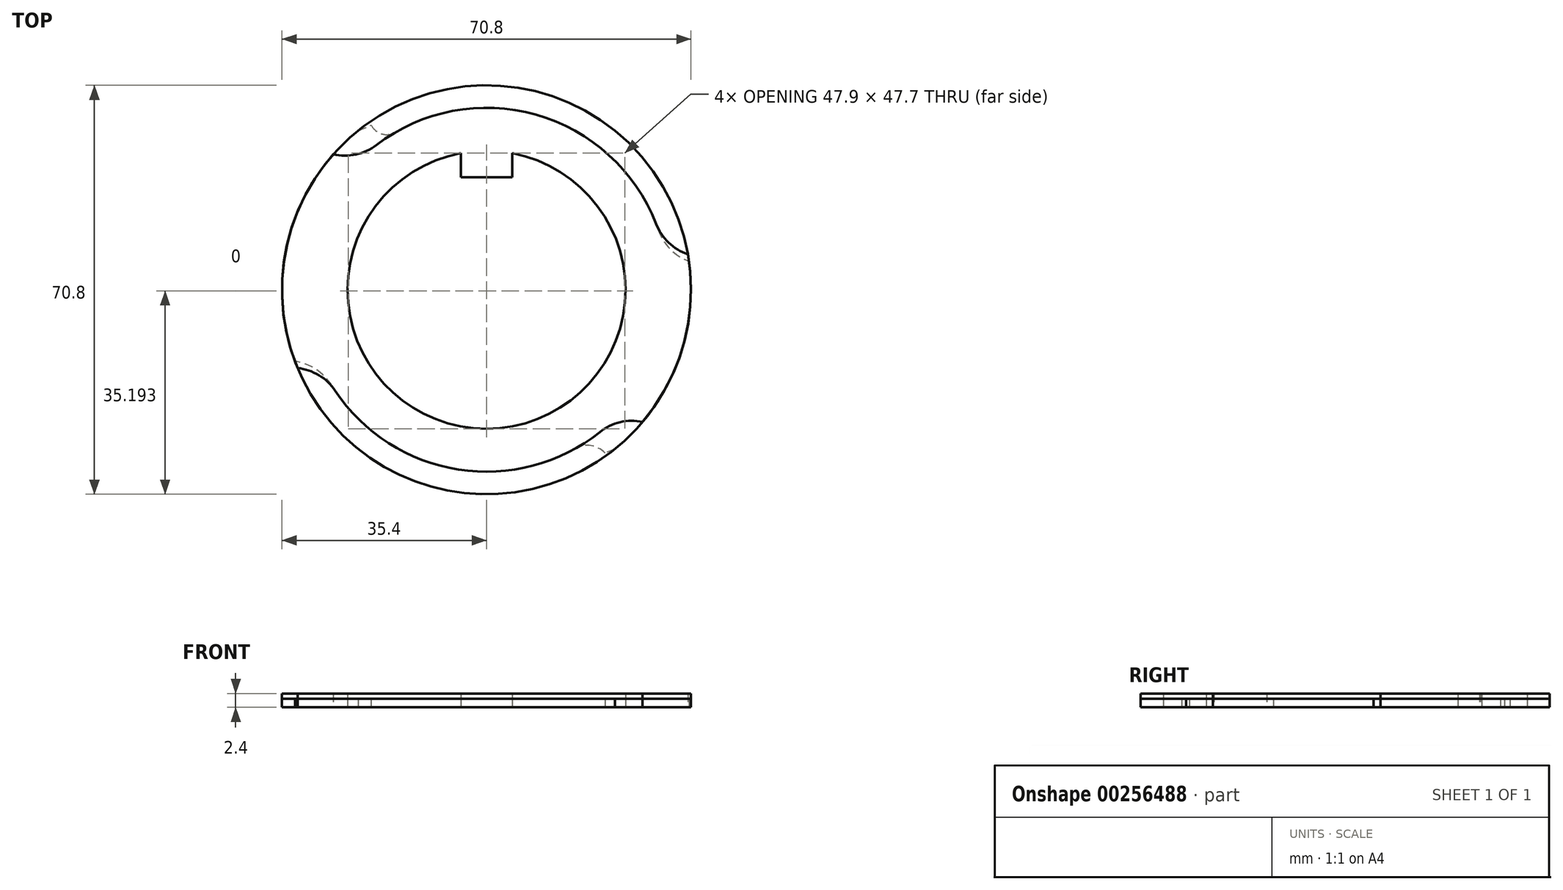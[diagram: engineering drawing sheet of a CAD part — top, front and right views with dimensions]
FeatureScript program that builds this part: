
annotation { "Feature Type Name" : "Feature", "Feature Type Description" : "" }
export const myFeature = defineFeature(function(context is Context, id is Id, definition is map)
    precondition{}
    {
        {
            var Q0;
            Q0=qCreatedBy(makeId("Top.planeOp"),FACE);
            var sketch = newSketch(context, id + "F0", { "sketchPlane" : qUnion([Q0])});
            skArc(sketch, "E0", {"start": v(7.4, -9.19) * mm, "mid": v(3.12, 11.38) * mm, "end": v(-11.05, -4.13) * mm});
            skArc(sketch, "E1", {"start": v(-1.48, 7.88) * mm, "mid": v(0, -8.02) * mm, "end": v(1.48, 7.88) * mm});
            skLineSegment(sketch, "E2", {"start": v(-1.48, 6.5) * mm, "end": v(1.48, 6.5) * mm});
            skPoint(sketch, "E3", {"position": v(0, 6.5) * mm});
            skLineSegment(sketch, "E4", {"start": v(1.48, 6.5) * mm, "end": v(1.48, 7.88) * mm});
            skLineSegment(sketch, "E5", {"start": v(-1.48, 6.5) * mm, "end": v(-1.48, 7.88) * mm});
            skLineSegment(sketch, "E6", {"start": v(0, 0) * mm, "end": v(6.94, -9.55) * mm, "construction": true});
            skLineSegment(sketch, "E7", {"start": v(0, 0) * mm, "end": v(-11.05, -4.13) * mm, "construction": true});
            skArc(sketch, "E8", {"start": v(-8.93, -5.52) * mm, "mid": v(-2.62, -10.17) * mm, "end": v(5.14, -9.15) * mm});
            skArc(sketch, "E9", {"start": v(-8.93, -5.52) * mm, "mid": v(-9.84, -4.6) * mm, "end": v(-11.05, -4.13) * mm});
            skArc(sketch, "E10", {"start": v(6.84, -9.43) * mm, "mid": v(6.04, -9) * mm, "end": v(5.14, -9.15) * mm});
            skLineSegment(sketch, "E11", {"start": v(7.4, -9.19) * mm, "end": v(6.84, -9.43) * mm});
            skSolve(sketch);
        }
        {
            var Q0;
            Q0=makeQuery(id+"F0.imprint","IMPRINT",FACE,{"disambiguationData":[TD([[makeQuery(id+"F0.imprint","IMPRINT",EDGE,{"derivedFrom":sQuery(id+"F0.wireOp",EDGE,"E0")}),1.0]])]});
            extrude(context, id + "F1", {"entities" : qUnion([Q0]), "depth" : 0.5 * mm});
        }
        {
            var Q0;
            Q0=qCreatedBy(makeId("Top.planeOp"),FACE);
            var sketch = newSketch(context, id + "F2", { "sketchPlane" : qUnion([Q0])});
            skArc(sketch, "E12", {"start": v(9, -7.62) * mm, "mid": v(1.82, 11.66) * mm, "end": v(-10.9, -4.52) * mm});
            skArc(sketch, "E13", {"start": v(-1.48, 7.88) * mm, "mid": v(0, -8.02) * mm, "end": v(1.48, 7.88) * mm});
            skLineSegment(sketch, "E14", {"start": v(-1.48, 6.5) * mm, "end": v(1.48, 6.5) * mm});
            skPoint(sketch, "E15", {"position": v(0, 6.5) * mm});
            skLineSegment(sketch, "E16", {"start": v(-1.48, 6.5) * mm, "end": v(-1.48, 7.88) * mm});
            skLineSegment(sketch, "E17", {"start": v(1.48, 6.5) * mm, "end": v(1.48, 7.88) * mm});
            skLineSegment(sketch, "E18", {"start": v(0, 0) * mm, "end": v(9, -7.62) * mm, "construction": true});
            skLineSegment(sketch, "E19", {"start": v(0, 0) * mm, "end": v(-10.9, -4.52) * mm, "construction": true});
            skArc(sketch, "E20", {"start": v(-8.73, -5.83) * mm, "mid": v(-1.62, -10.37) * mm, "end": v(6.54, -8.22) * mm});
            skArc(sketch, "E21", {"start": v(-8.73, -5.83) * mm, "mid": v(-9.67, -4.93) * mm, "end": v(-10.9, -4.52) * mm});
            skArc(sketch, "E22", {"start": v(9, -7.62) * mm, "mid": v(7.7, -7.65) * mm, "end": v(6.54, -8.22) * mm});
            skPoint(sketch, "E23.orphan", {"position": v(-9.7, -4.02) * mm});
            skPoint(sketch, "E24.orphan", {"position": v(8.01, -6.78) * mm});
            skSolve(sketch);
        }
        {
            var Q0;
            Q0=makeQuery(id+"F2.imprint","IMPRINT",FACE,{"disambiguationData":[TD([[makeQuery(id+"F2.imprint","IMPRINT",EDGE,{"derivedFrom":sQuery(id+"F2.wireOp",EDGE,"E12")}),1.0]])]});
            extrude(context, id + "F3", {"entities" : qUnion([Q0]), "depth" : 0.8 * mm});
        }
        {
            var Q0;
            Q0=qCreatedBy(makeId("Top.planeOp"),FACE);
            var sketch = newSketch(context, id + "F4", { "sketchPlane" : qUnion([Q0])});
            skArc(sketch, "E25", {"start": v(-1.48, 7.88) * mm, "mid": v(0, -8.02) * mm, "end": v(1.48, 7.88) * mm});
            skArc(sketch, "E26", {"start": v(-7.4, 9.19) * mm, "mid": v(-4.34, -10.97) * mm, "end": v(11.69, 1.64) * mm});
            skLineSegment(sketch, "E27", {"start": v(-1.48, 6.5) * mm, "end": v(1.48, 6.5) * mm});
            skPoint(sketch, "E28", {"position": v(0, 6.5) * mm});
            skLineSegment(sketch, "E29", {"start": v(-1.48, 6.5) * mm, "end": v(-1.48, 7.88) * mm});
            skLineSegment(sketch, "E30", {"start": v(1.48, 6.5) * mm, "end": v(1.48, 7.88) * mm});
            skLineSegment(sketch, "E31", {"start": v(0, 0) * mm, "end": v(-6.73, 9.7) * mm, "construction": true});
            skLineSegment(sketch, "E32", {"start": v(0, 0) * mm, "end": v(11.69, 1.64) * mm, "construction": true});
            skArc(sketch, "E33", {"start": v(9.91, 3.46) * mm, "mid": v(3.65, 9.84) * mm, "end": v(-5.26, 9.09) * mm});
            skArc(sketch, "E34", {"start": v(-6.65, 9.5) * mm, "mid": v(-6.05, 9) * mm, "end": v(-5.26, 9.09) * mm});
            skArc(sketch, "E35", {"start": v(9.91, 3.46) * mm, "mid": v(10.6, 2.35) * mm, "end": v(11.69, 1.64) * mm});
            skLineSegment(sketch, "E36", {"start": v(-7.4, 9.19) * mm, "end": v(-6.65, 9.5) * mm});
            skSolve(sketch);
        }
        {
            var Q0;
            Q0=makeQuery(id+"F4.imprint","IMPRINT",FACE,{"disambiguationData":[TD([[makeQuery(id+"F4.imprint","IMPRINT",EDGE,{"derivedFrom":sQuery(id+"F4.wireOp",EDGE,"E25")}),-1.0]])]});
            extrude(context, id + "F5", {"entities" : qUnion([Q0]), "depth" : 0.5 * mm});
        }
        {
            var Q0;
            Q0=qCreatedBy(makeId("Top.planeOp"),FACE);
            var sketch = newSketch(context, id + "F6", { "sketchPlane" : qUnion([Q0])});
            skArc(sketch, "E37", {"start": v(-1.48, 7.88) * mm, "mid": v(0, -8.02) * mm, "end": v(1.48, 7.88) * mm});
            skArc(sketch, "E38", {"start": v(-8.84, 7.82) * mm, "mid": v(-3.2, -11.36) * mm, "end": v(11.62, 2.05) * mm});
            skLineSegment(sketch, "E39", {"start": v(-1.48, 6.5) * mm, "end": v(1.48, 6.5) * mm});
            skPoint(sketch, "E40", {"position": v(0, 6.5) * mm});
            skLineSegment(sketch, "E41", {"start": v(-1.48, 6.5) * mm, "end": v(-1.48, 7.88) * mm});
            skLineSegment(sketch, "E42", {"start": v(1.48, 6.5) * mm, "end": v(1.48, 7.88) * mm});
            skLineSegment(sketch, "E43", {"start": v(0, 0) * mm, "end": v(-8.84, 7.82) * mm, "construction": true});
            skLineSegment(sketch, "E44", {"start": v(0, 0) * mm, "end": v(11.62, 2.05) * mm, "construction": true});
            skArc(sketch, "E45", {"start": v(9.79, 3.8) * mm, "mid": v(2.85, 10.1) * mm, "end": v(-6.36, 8.36) * mm});
            skArc(sketch, "E46", {"start": v(-8.84, 7.82) * mm, "mid": v(-7.54, 7.81) * mm, "end": v(-6.36, 8.36) * mm});
            skArc(sketch, "E47", {"start": v(9.79, 3.8) * mm, "mid": v(10.5, 2.72) * mm, "end": v(11.62, 2.05) * mm});
            skSolve(sketch);
        }
        {
            var Q0;
            Q0=makeQuery(id+"F6.imprint","IMPRINT",FACE,{"disambiguationData":[TD([[makeQuery(id+"F6.imprint","IMPRINT",EDGE,{"derivedFrom":sQuery(id+"F6.wireOp",EDGE,"E37")}),-1.0]])]});
            extrude(context, id + "F7", {"entities" : qUnion([Q0]), "depth" : 0.8 * mm});
        }
        {
            var Q0;
            Q0=makeQuery(id+"F1.opExtrude","SWEPT_BODY",BODY,{"disambiguationData":[OSD([sQuery(id+"F0.wireOp",EDGE,"E0"),sQuery(id+"F0.wireOp",EDGE,"E1"),sQuery(id+"F0.wireOp",EDGE,"E2"),sQuery(id+"F0.wireOp",EDGE,"E4"),sQuery(id+"F0.wireOp",EDGE,"E5"),sQuery(id+"F0.wireOp",EDGE,"E8"),sQuery(id+"F0.wireOp",EDGE,"E9"),sQuery(id+"F0.wireOp",EDGE,"E10"),sQuery(id+"F0.wireOp",EDGE,"E11")])]});
            var Q1;
            Q1=makeQuery(id+"F3.opExtrude","SWEPT_BODY",BODY,{"disambiguationData":[OSD([sQuery(id+"F2.wireOp",EDGE,"E12"),sQuery(id+"F2.wireOp",EDGE,"E13"),sQuery(id+"F2.wireOp",EDGE,"E14"),sQuery(id+"F2.wireOp",EDGE,"E16"),sQuery(id+"F2.wireOp",EDGE,"E17"),sQuery(id+"F2.wireOp",EDGE,"E20"),sQuery(id+"F2.wireOp",EDGE,"E21"),sQuery(id+"F2.wireOp",EDGE,"E22")])]});
            var Q2;
            Q2=makeQuery(id+"F5.opExtrude","SWEPT_BODY",BODY,{"disambiguationData":[OSD([sQuery(id+"F4.wireOp",EDGE,"E25"),sQuery(id+"F4.wireOp",EDGE,"E26"),sQuery(id+"F4.wireOp",EDGE,"E27"),sQuery(id+"F4.wireOp",EDGE,"E29"),sQuery(id+"F4.wireOp",EDGE,"E30"),sQuery(id+"F4.wireOp",EDGE,"E33"),sQuery(id+"F4.wireOp",EDGE,"E34"),sQuery(id+"F4.wireOp",EDGE,"E35"),sQuery(id+"F4.wireOp",EDGE,"E36")])]});
            var Q3;
            Q3=makeQuery(id+"F7.opExtrude","SWEPT_BODY",BODY,{"disambiguationData":[OSD([sQuery(id+"F6.wireOp",EDGE,"E37"),sQuery(id+"F6.wireOp",EDGE,"E38"),sQuery(id+"F6.wireOp",EDGE,"E39"),sQuery(id+"F6.wireOp",EDGE,"E41"),sQuery(id+"F6.wireOp",EDGE,"E42"),sQuery(id+"F6.wireOp",EDGE,"E45"),sQuery(id+"F6.wireOp",EDGE,"E46"),sQuery(id+"F6.wireOp",EDGE,"E47")])]});
            var Q4;
            Q4=qCreatedBy(makeId("Origin.pointOp"),VERTEX);
            transform(context, id + "F8", {"entities" : qUnion([Q0, Q1, Q2, Q3]), "transformType" : TransformType.SCALE_UNIFORMLY, "scale" : 3, "makeCopy" : false, "scalePoint" : qUnion([Q4])});
        }
    });
